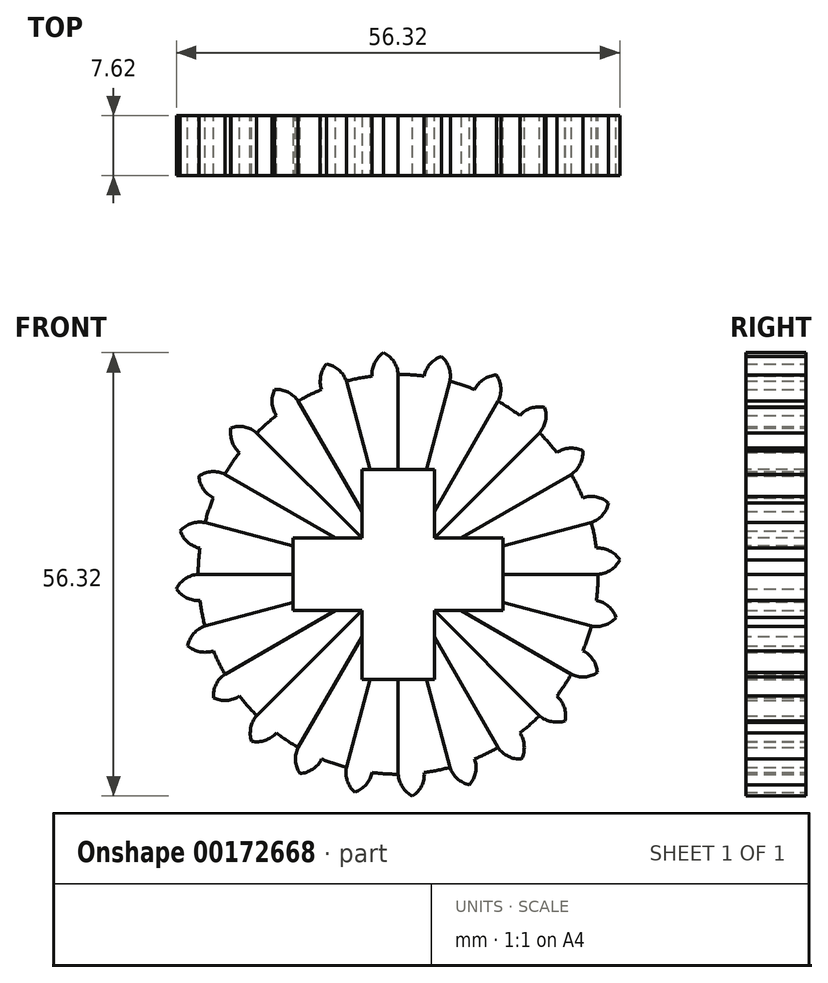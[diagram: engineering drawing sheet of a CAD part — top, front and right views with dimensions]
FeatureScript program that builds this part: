
annotation { "Feature Type Name" : "Feature", "Feature Type Description" : "" }
export const myFeature = defineFeature(function(context is Context, id is Id, definition is map)
    precondition{}
    {
        {
            var Q0;
            Q0=qCreatedBy(makeId("Front.planeOp"),FACE);
            var sketch = newSketch(context, id + "F0", { "sketchPlane" : qUnion([Q0])});
            skLineSegment(sketch, "E0", {"start": v(0, 0) * mm, "end": v(25.4, 0) * mm});
            skLineSegment(sketch, "E1", {"start": v(0, 0) * mm, "end": v(24.53, 6.57) * mm});
            skArc(sketch, "E2", {"start": v(25.4, 0) * mm, "mid": v(25.18, 3.32) * mm, "end": v(24.53, 6.57) * mm});
            skLineSegment(sketch, "E3", {"start": v(0, 0) * mm, "end": v(24.75, 3.26) * mm, "construction": true});
            skLineSegment(sketch, "E4", {"start": v(0, 0) * mm, "end": v(25.35, 1.66) * mm, "construction": true});
            skArc(sketch, "E5", {"start": v(28.16, 1.85) * mm, "mid": v(26.87, 2.98) * mm, "end": v(25.18, 3.32) * mm});
            skArc(sketch, "E6.trimOffspring", {"start": v(25.4, 0) * mm, "mid": v(27.03, 0.55) * mm, "end": v(28.16, 1.85) * mm});
            skSolve(sketch);
        }
        {
            var Q0;
            {var subQ0=sQuery(id+"F0.wireOp",EDGE,"f65f0aed-6f73-4a8c-9e57-06b89b6f523b.trimOffspring");Q0=makeQuery(id+"F0.imprint","IMPRINT",FACE,{"disambiguationData":[TD([[makeQuery(id+"F0.imprint","IMPRINT",EDGE,{"derivedFrom":subQ0}),1.0]])]});}
            var Q1;
            {var subQ0=sQuery(id+"F0.wireOp",EDGE,"E0");Q1=makeQuery(id+"F0.imprint","IMPRINT",FACE,{"disambiguationData":[TD([[makeQuery(id+"F0.imprint","IMPRINT",EDGE,{"derivedFrom":subQ0}),1.0]])]});}
            var Q2;
            {var subQ2=sQuery(id+"F0.wireOp",EDGE,"E5");Q2=makeQuery(id+"F0.imprint","IMPRINT",FACE,{"disambiguationData":[TD([[makeQuery(id+"F0.imprint","IMPRINT",EDGE,{"derivedFrom":subQ2}),1.0]])]});}
            extrude(context, id + "F1", {"entities" : qUnion([Q0, Q1, Q2]), "depth" : 7.62 * mm});
        }
        {
            var Q0;
            Q0=makeQuery(id+"F1.opExtrude","SWEPT_BODY",BODY,{"disambiguationData":[OSD([sQuery(id+"F0.wireOp",EDGE,"E0"),sQuery(id+"F0.wireOp",EDGE,"E1"),sQuery(id+"F0.wireOp",EDGE,"E2"),sQuery(id+"F0.wireOp",EDGE,"f65f0aed-6f73-4a8c-9e57-06b89b6f523b.trimOffspring"),sQuery(id+"F0.wireOp",EDGE,"0ac6d69e-e550-4225-a946-7005ccabb6f8.trimOffspring")])]});
            var Q1;
            Q1=makeQuery(id+"F1.opExtrude","SWEPT_EDGE",EDGE,{"disambiguationData":[OSD([sQuery(id+"F0.wireOp",EDGE,"E0"),sQuery(id+"F0.wireOp",EDGE,"E1")])]});
            circularPattern(context, id + "F2", {"entities" : qUnion([Q0]), "axis" : qUnion([Q1]), "angle" : 15 * degree, "instanceCount" : 24});
        }
        {
            var Q0;
            Q0=qCreatedBy(makeId("Front.planeOp"),FACE);
            var sketch = newSketch(context, id + "F3", { "sketchPlane" : qUnion([Q0])});
            skLineSegment(sketch, "E7.bottom", {"start": v(13.34, 4.61) * mm, "end": v(-13.34, 4.61) * mm});
            skLineSegment(sketch, "E7.top", {"start": v(13.34, -4.61) * mm, "end": v(-13.34, -4.61) * mm});
            skLineSegment(sketch, "E7.left", {"start": v(13.34, 4.61) * mm, "end": v(13.34, -4.61) * mm});
            skLineSegment(sketch, "E7.right", {"start": v(-13.34, 4.61) * mm, "end": v(-13.34, -4.61) * mm});
            skPoint(sketch, "E7.middle", {"position": v(0, 0) * mm});
            skLineSegment(sketch, "E8.bottom", {"start": v(4.61, 13.34) * mm, "end": v(-4.61, 13.34) * mm});
            skLineSegment(sketch, "E8.top", {"start": v(4.61, -13.34) * mm, "end": v(-4.61, -13.34) * mm});
            skLineSegment(sketch, "E8.left", {"start": v(4.61, 13.34) * mm, "end": v(4.61, -13.34) * mm});
            skLineSegment(sketch, "E8.right", {"start": v(-4.61, 13.34) * mm, "end": v(-4.61, -13.34) * mm});
            skSolve(sketch);
        }
        {
            var Q0;
            Q0=qSketchRegion(id+"F3",true);
            extrude(context, id + "F4", {"entities" : qUnion([Q0]), "operationType" : NewBodyOperationType.REMOVE, "depth" : 25.4 * mm});
        }
    });
